# Revit family: EDE-GRF-LVM_Roma Llave Sencilla para Lavamanos
name_source: partatom
category: Aparatos sanitarios
units: mm (PartAtom-declared; Revit-internal decimal feet)

## family parameters
Compartido = Sí
Corte con vacíos al cargar = No
Cota de conector redondo = Diámetro de uso
Número OmniClass = 23.45.00.00
Punto de cálculo de habitación = Sí
Se basa en plano de trabajo = No
Siempre vertical = Sí
Tipo de pieza = Normal
Título OmniClass = Sanitary, Laundry, and Cleaning Equipment

## types (1)
- Roma Llave Sencilla para Lavamanos
    Conexión AC = Sí
    Conexión AF = Sí
    Conexión de residuos = Sí
    Conexión de ventilación = Sí
    Elevación por defecto = 0 m
    Fabricante = EDESA Ecuador
    Imagen de tipo = <Ninguno>
    Modelo = Roma Llave Sencilla para Lavamanos
    URL = https://www.edesa.com.ec
    _ALT_Toma = 0.55 m
    _EDESA_ Alto en cm = 16.7
    _EDESA_ Ancho en cm = 4.4
    _EDESA_ Categoría = Productos > Grifería > Lavamanos
    _EDESA_ Certificación = Cumple con norma NTE - INEN 3123 basada en la norma ASME 112.18.1 - 2012.
    _EDESA_ Color = cromo
    _EDESA_ Conexión hidráulica = Entrada de agua: tubería ø 1/2" Salida de agua: tubería PVC 50
    _EDESA_ Consumo/capacidad de agua en L = 8.3 litros por minuto / 2.2 gpm a 60 psi
    _EDESA_ Descripción = Llave de lavamanos para agua fría. Instalación sobre lavamanos
    _EDESA_ Garantía = De por vida para el cuerpo principal y acabado en cromo (306)
    _EDESA_ Manual de instalación = https://www.edesa.com.ec
    _EDESA_ Materiales = ABS Cromado
    _EDESA_ Nombre = ROMA LLAVE SENCILLA PARA LAVAMANOS
    _EDESA_ Productos necesarios para instalación = Desagüe, Sifón, Llave angular y manguera flexible
    _EDESA_ Profundidad en cm = 11.7
    _EDESA_ Sku/código = SG0074340001BO
    _EDESA_ Tipo de instalación = Sobre lavamanos
